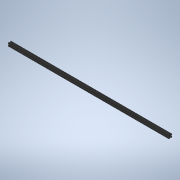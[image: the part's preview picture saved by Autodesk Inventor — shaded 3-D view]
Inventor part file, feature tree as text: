
AUTODESK INVENTOR PART (.ipt)
format: ipt  version: 2021 (Build 250183000, 183)  size: 163,328 bytes
history: native  units: mm
features: extrude x1, sketch x1
ambient origin geometry x8: Origin, YZ Plane, XZ Plane, XY Plane, X Axis, Y Axis, Z Axis, Center Point
bodies: Solid1 (feature_tree)
feature tree (2):
  extrude  "Extrusion1"  [1 undecoded]
  sketch  "Skizze_1"  dims[d0=1300.0mm d1=0.0mm]
note: 1 required parameter value undecoded (feature->parameter linkage not recoverable at this tier; creation-order binding heuristic only, values carry confidence <= 0.55)
